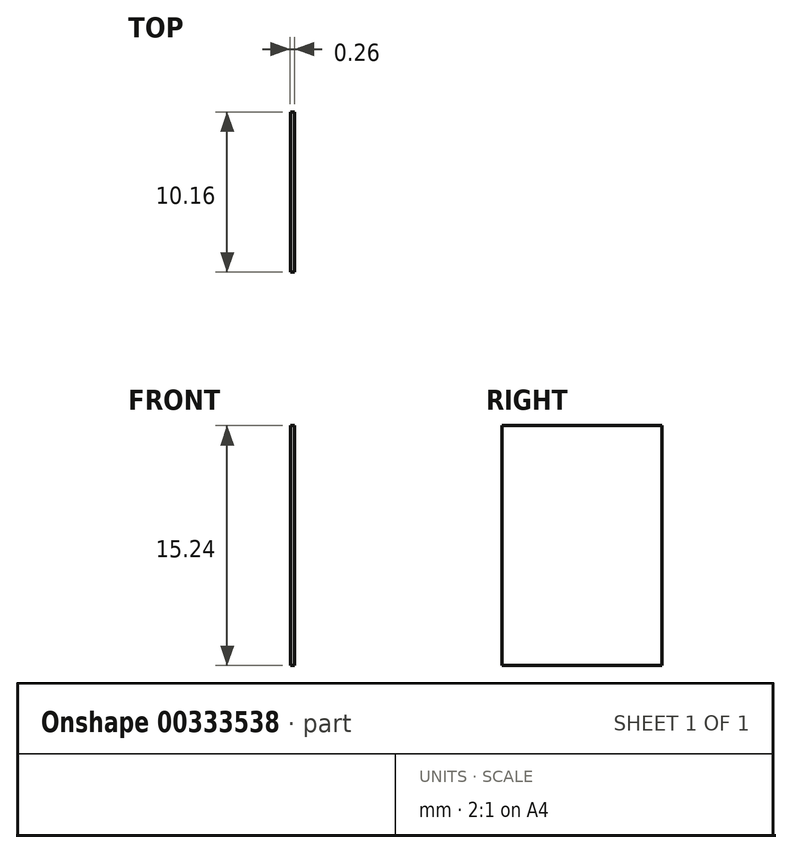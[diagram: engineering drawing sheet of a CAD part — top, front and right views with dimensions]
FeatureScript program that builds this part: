
annotation { "Feature Type Name" : "Feature", "Feature Type Description" : "" }
export const myFeature = defineFeature(function(context is Context, id is Id, definition is map)
    precondition{}
    {
        {
            var Q0;
            Q0=qCreatedBy(makeId("Right.planeOp"),FACE);
            var sketch = newSketch(context, id + "F0", { "sketchPlane" : qUnion([Q0])});
            skLineSegment(sketch, "E0.bottom", {"start": v(-5.08, 7.62) * mm, "end": v(5.08, 7.62) * mm});
            skLineSegment(sketch, "E0.top", {"start": v(-5.08, -7.62) * mm, "end": v(5.08, -7.62) * mm});
            skLineSegment(sketch, "E0.left", {"start": v(-5.08, 7.62) * mm, "end": v(-5.08, -7.62) * mm});
            skLineSegment(sketch, "E0.right", {"start": v(5.08, 7.62) * mm, "end": v(5.08, -7.62) * mm});
            skPoint(sketch, "E0.middle", {"position": v(0, 0) * mm});
            skSolve(sketch);
        }
        {
            var Q0;
            Q0 = qSketchRegion(id + "F0", true);
            extrude(context, id + "F1", {"entities" : qUnion([Q0]), "depth" : 0.25 * mm, "offsetDistance" : 25.4 * mm, "symmetric" : true});
        }
    });
